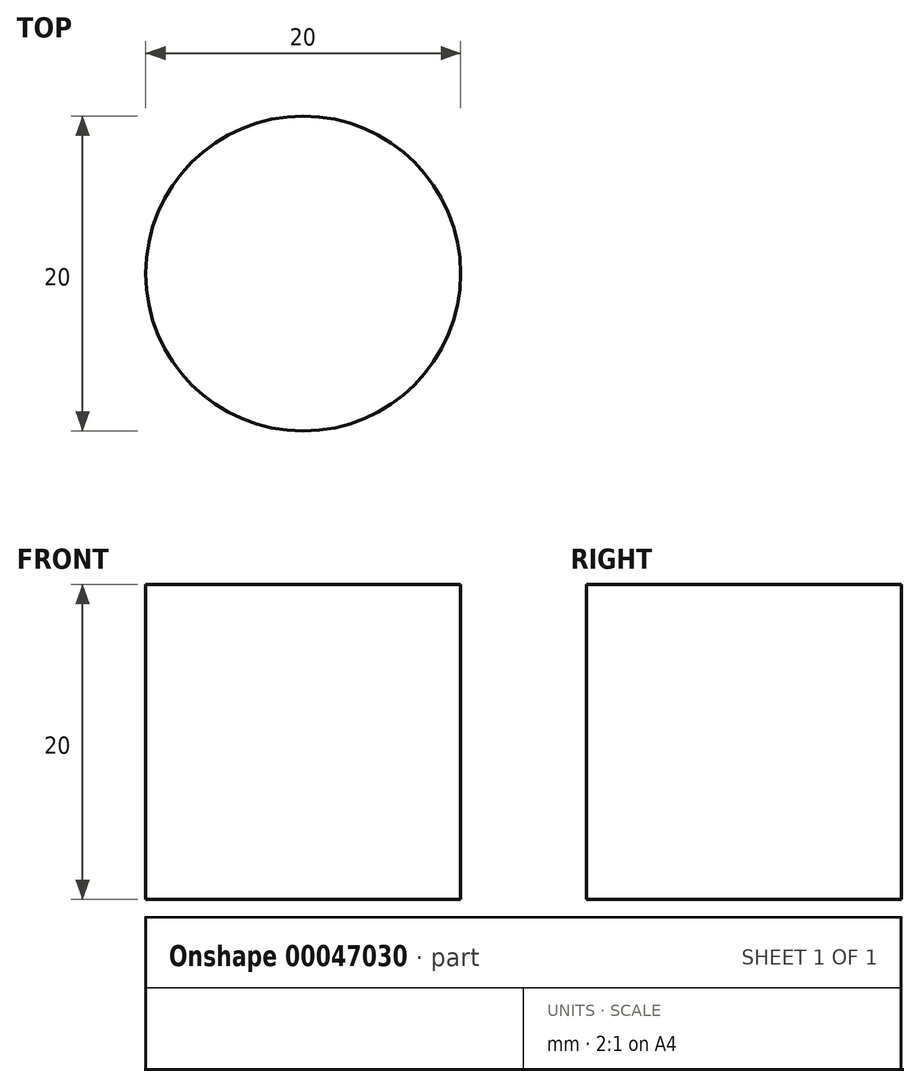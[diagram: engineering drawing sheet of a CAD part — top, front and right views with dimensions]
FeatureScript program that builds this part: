
annotation { "Feature Type Name" : "Feature", "Feature Type Description" : "" }
export const myFeature = defineFeature(function(context is Context, id is Id, definition is map)
    precondition{}
    {
        {
            var Q0;
            Q0=qCreatedBy(makeId("Top.planeOp"),FACE);
            var sketch = newSketch(context, id + "F0", { "sketchPlane" : qUnion([Q0])});
            skCircle(sketch, "E0", {"center": v(0, 0) * mm, "radius": 10 * mm});
            skSolve(sketch);
        }
        {
            var Q0;
            Q0 = qSketchRegion(id + "F0", true);
            extrude(context, id + "F1", {"entities" : qUnion([Q0]), "depth" : 20 * mm});
        }
    });
